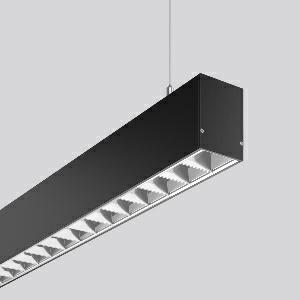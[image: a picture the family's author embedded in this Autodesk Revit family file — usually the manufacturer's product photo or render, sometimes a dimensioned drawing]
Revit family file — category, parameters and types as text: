
# Revit family: less_is_more_50_312339_003_1_76_0224
name_source: partatom
category: Lighting Fixtures
units: mm (PartAtom-declared; Revit-internal decimal feet)

## family parameters
Cut with Voids When Loaded = No
Host = Face
Light Source = No
Part Type = Normal
Room Calculation Point = No
Round Connector Dimension = Use Diameter
Shared = No

## types (1)
- LESS IS MORE 50 (1 x LED Modul 840, 6200 lm, 4000)
    Apparent Load = 48 VA
    CIE Flux Codes = 95 100 100 100 100
    Color Rendering = 80
    Color Temperature = 4000
    Default Elevation = 1800 mm
    Description = Series: LESS IS MORE 50
Linear pendant luminaire for aesthetically sophisticated lighting. Housing: extruded aluminium profile, powder-coated. End cap aluminium powder-coated. Canopy made of aluminium, powder-coated. Alea optical system: Reflector structure (ABS, Aluminium-coated, highly polished) with integrated diffuser made of non-yellowing plastic (PMMA) opal for glare-free light at the workstation (screen-compliant according to EN 12464-1). Direct light emission. Suitable for pendant. 2-point steel cable suspension freely positionable and infinitely height-adjustable. Special lengths available on request. LED unit with integrated converter interchangeable and removable. Suitable for through-wiring. With sensors or as a safety luminaire on request. 
Colour: deep black, matt (RAL 9005)
Length: 1967 mm
Width: 57 mm
Height: 75 mm
Suspension length: 2000 mm
Lamp: LED
Socket: without socket
Colour temperature: 4000K
Colour rendering index (CRI): 80
System power: 48 W
Rated luminous flux: 6200 lm
Luminous efficiency: 129 lm/W
Control gear: Converter, dimmable, DALI
Protection class: I
Type of protection: IP 20
    Height = 75 mm
    Lamp = 1 x LED Modul 840
    Lamp Light Flux = 6200 lm
    Lamp count = 1
    Length = 1967 mm
    Lifetime = 50000 h
    Luminous efficacy = 129 lm/W
    Manufacturer = RZB
    ModVariant = No
    Model = 312339.003.1.76
    Mounting Place = Ceiling
    Mounting Type = Pendant
    Number of Poles = 1
    OnlyDefault = Yes
    Power Factor = 1
    Product Name = LESS IS MORE 50
    Product group = Pendant LED linear luminaires
    ProductGroupID = 907
    Protection Class = Protection class I
    Protection Degree = IP 20
    RLX_Detail_Level = 1
    RLX_Emergency_Light_Flux = 0 lm
    RLX_Emergency_Type = 0
    RLX_Emergency_Type_DB = No
    RlxData = <blob elided: 39549 chars, md5=b57dc704>
    Socket = socket
    Standby Power = 0 W
    System Light Flux = 6200 lm
    System Power = 48 W
    Type Comments = Product without accessories
    Type Image = 312342.003.jpg
    URL = http://relux.com
    VarID = ---
    Voltage = 230 V
    Voltage Range = 220-240 V
    Weight = 0.00 kg
    Width = 57 mm

## geometry (parser evidence)
native form markers: Blend x4, Sweep x9
no freeform markers — native parametric forms only
